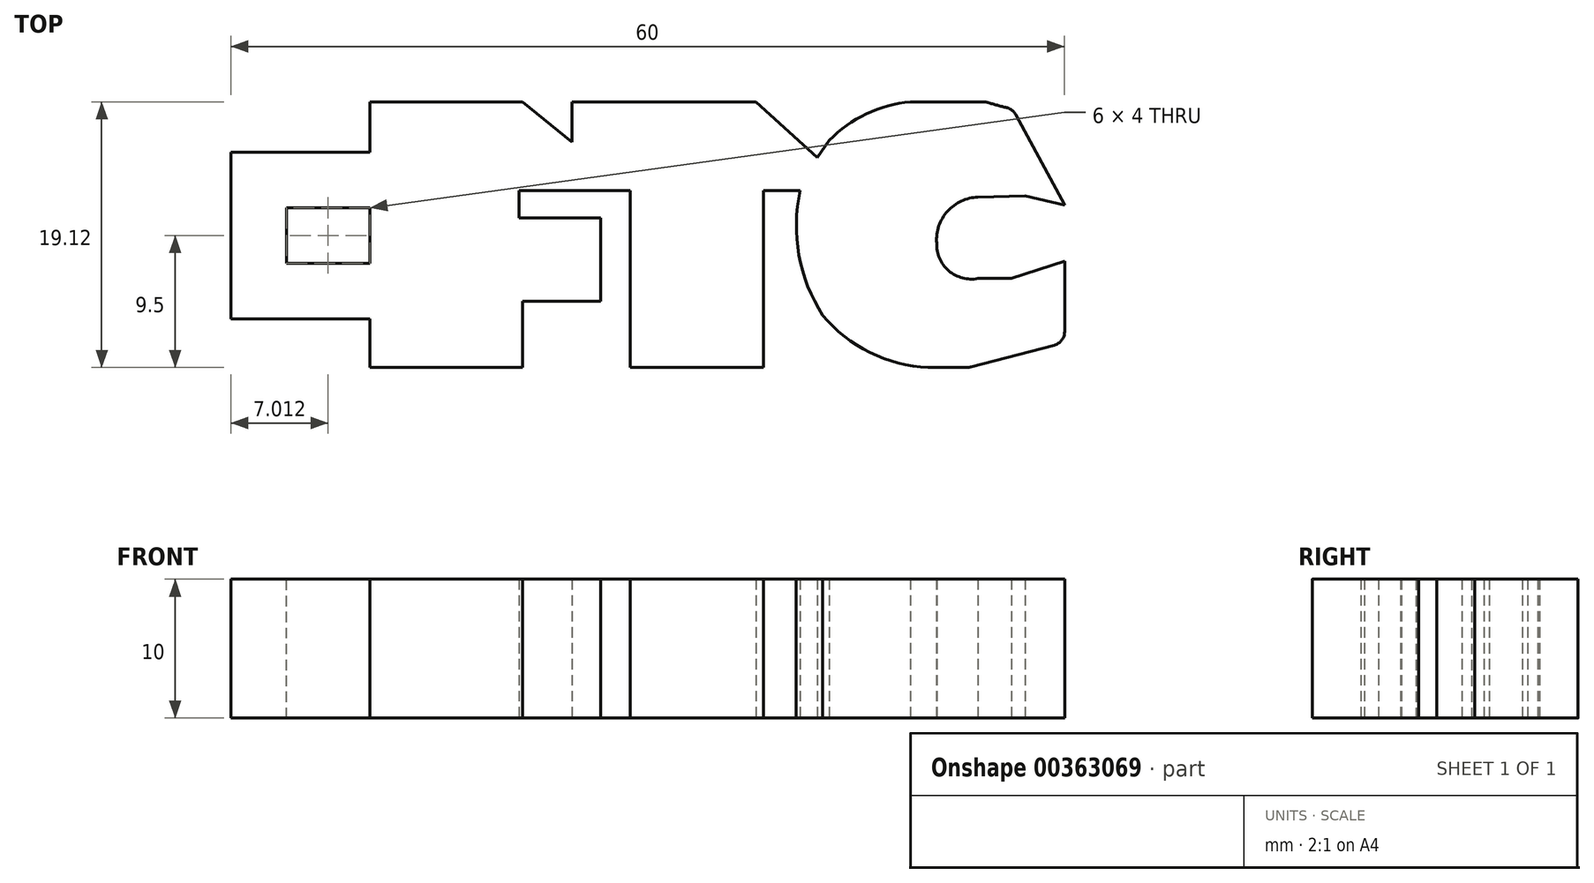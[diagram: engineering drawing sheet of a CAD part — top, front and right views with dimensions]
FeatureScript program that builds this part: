
annotation { "Feature Type Name" : "Feature", "Feature Type Description" : "" }
export const myFeature = defineFeature(function(context is Context, id is Id, definition is map)
    precondition{}
    {
        {
            var Q0;
            Q0=qCreatedBy(makeId("Top.planeOp"),FACE);
            var sketch = newSketch(context, id + "F0", { "sketchPlane" : qUnion([Q0])});
            skLineSegment(sketch, "E0", {"start": v(-22.32, 9.12) * mm, "end": v(-11.34, 9.12) * mm});
            skLineSegment(sketch, "E1", {"start": v(-22.32, 9.12) * mm, "end": v(-22.32, -10) * mm});
            skLineSegment(sketch, "E2", {"start": v(-22.32, -10) * mm, "end": v(-11.33, -10) * mm});
            skLineSegment(sketch, "E3", {"start": v(27.68, 1.7) * mm, "end": v(23.95, 8.6) * mm});
            skLineSegment(sketch, "E4", {"start": v(-7.76, 6.22) * mm, "end": v(-11.34, 9.12) * mm});
            skLineSegment(sketch, "E5", {"start": v(-7.76, 9.12) * mm, "end": v(-7.76, 6.22) * mm});
            skLineSegment(sketch, "E6", {"start": v(9.88, 5.1) * mm, "end": v(5.48, 9.12) * mm});
            skLineSegment(sketch, "E7", {"start": v(-11.56, 2.74) * mm, "end": v(-3.57, 2.74) * mm});
            skLineSegment(sketch, "E8", {"start": v(-11.56, 0.76) * mm, "end": v(-5.71, 0.76) * mm});
            skLineSegment(sketch, "E9", {"start": v(-11.56, 2.74) * mm, "end": v(-11.56, 0.76) * mm});
            skLineSegment(sketch, "E10", {"start": v(6.01, 2.74) * mm, "end": v(8.65, 2.74) * mm});
            skArc(sketch, "E11", {"start": v(22.01, 9.12) * mm, "mid": v(22.98, 8.84) * mm, "end": v(23.95, 8.6) * mm});
            skLineSegment(sketch, "E12", {"start": v(9.88, 5.1) * mm, "end": v(10.76, 6.34) * mm});
            skArc(sketch, "E13", {"start": v(16.58, 9.12) * mm, "mid": v(13.42, 8.26) * mm, "end": v(10.76, 6.34) * mm});
            skLineSegment(sketch, "E14", {"start": v(-11.33, -5.25) * mm, "end": v(-5.71, -5.25) * mm});
            skLineSegment(sketch, "E15", {"start": v(-11.33, -10) * mm, "end": v(-11.33, -5.25) * mm});
            skLineSegment(sketch, "E16", {"start": v(-3.57, 2.74) * mm, "end": v(-3.57, -10) * mm});
            skLineSegment(sketch, "E17", {"start": v(27.68, -8.2) * mm, "end": v(20.82, -10) * mm});
            skArc(sketch, "E18", {"start": v(8.65, 2.74) * mm, "mid": v(8.57, -1.91) * mm, "end": v(10.28, -6.24) * mm});
            skArc(sketch, "E19", {"start": v(10.28, -6.24) * mm, "mid": v(14.06, -9.1) * mm, "end": v(18.73, -10) * mm});
            skArc(sketch, "E20", {"start": v(21.45, 2.26) * mm, "mid": v(19.26, 1.25) * mm, "end": v(18.48, -1.04) * mm});
            skArc(sketch, "E21", {"start": v(18.48, -1.04) * mm, "mid": v(19.35, -3.04) * mm, "end": v(21.45, -3.6) * mm});
            skLineSegment(sketch, "E22", {"start": v(21.45, -3.6) * mm, "end": v(23.85, -3.6) * mm});
            skLineSegment(sketch, "E23", {"start": v(23.85, -3.6) * mm, "end": v(27.68, -2.34) * mm});
            skLineSegment(sketch, "E24", {"start": v(21.45, 2.26) * mm, "end": v(24.84, 2.36) * mm});
            skLineSegment(sketch, "E25", {"start": v(24.84, 2.36) * mm, "end": v(27.68, 1.68) * mm});
            skLineSegment(sketch, "E26", {"start": v(6.01, 2.74) * mm, "end": v(6.01, -10) * mm});
            skPoint(sketch, "E27.orphan", {"position": v(-11.56, 0) * mm});
            skLineSegment(sketch, "E28.trimOffspring", {"start": v(-5.71, 0.76) * mm, "end": v(-5.71, -5.25) * mm});
            skPoint(sketch, "E29.orphan", {"position": v(-2.04, 2.74) * mm});
            skPoint(sketch, "E30.orphan", {"position": v(-22.32, -12.38) * mm});
            skPoint(sketch, "E31.orphan", {"position": v(-26.16, -10) * mm});
            skPoint(sketch, "E32.orphan", {"position": v(5.02, 2.74) * mm});
            skPoint(sketch, "E33.orphan", {"position": v(10.28, 2.74) * mm});
            skLineSegment(sketch, "E34.trimOffspring", {"start": v(27.68, -8.2) * mm, "end": v(27.68, -2.34) * mm});
            skPoint(sketch, "E35.start.orphan", {"position": v(27.68, -12.38) * mm});
            skLineSegment(sketch, "E36.trimOffspring", {"start": v(17.9, -10) * mm, "end": v(20.82, -10) * mm});
            skLineSegment(sketch, "E37.trimOffspring", {"start": v(-3.57, -10) * mm, "end": v(6.01, -10) * mm});
            skLineSegment(sketch, "E38.trimOffspring", {"start": v(27.68, 1.68) * mm, "end": v(27.68, 1.7) * mm});
            skPoint(sketch, "E39.orphan", {"position": v(27.68, 15.76) * mm});
            skLineSegment(sketch, "E40.trimOffspring", {"start": v(-7.76, 9.12) * mm, "end": v(5.48, 9.12) * mm});
            skLineSegment(sketch, "E41.trimOffspring", {"start": v(16.58, 9.12) * mm, "end": v(22.01, 9.12) * mm});
            skSolve(sketch);
        }
        {
            var Q0;
            Q0=makeQuery(id+"F0.imprint","IMPRINT",FACE,{"disambiguationData":[TD([[makeQuery(id+"F0.imprint","IMPRINT",EDGE,{"derivedFrom":sQuery(id+"F0.wireOp",EDGE,"E0")}),-1.0]])]});
            extrude(context, id + "F1", {"entities" : qUnion([Q0]), "depth" : 10 * mm});
        }
        {
            var Q0;
            Q0=makeQuery(id+"F1.opExtrude","SWEPT_EDGE",EDGE,{"disambiguationData":[OSD([sQuery(id+"F0.wireOp",EDGE,"E3"),sQuery(id+"F0.wireOp",EDGE,"E11")])]});
            var Q1;
            Q1=makeQuery(id+"F1.opExtrude","SWEPT_EDGE",EDGE,{"disambiguationData":[OSD([sQuery(id+"F0.wireOp",EDGE,"E11"),sQuery(id+"F0.wireOp",EDGE,"E41.trimOffspring")])]});
            fillet(context, id + "F2", {"entities" : qUnion([Q0, Q1]), "radius" : 1 * mm, "tangentPropagation" : true, "allowEdgeOverflow" : false});
        }
        {
            var Q0;
            Q0=makeQuery(id+"F1.opExtrude","SWEPT_EDGE",EDGE,{"disambiguationData":[OSD([sQuery(id+"F0.wireOp",EDGE,"E19"),sQuery(id+"F0.wireOp",EDGE,"E36.trimOffspring")])]});
            var Q1;
            Q1=makeQuery(id+"F1.opExtrude","SWEPT_EDGE",EDGE,{"disambiguationData":[OSD([sQuery(id+"F0.wireOp",EDGE,"E17"),sQuery(id+"F0.wireOp",EDGE,"E36.trimOffspring")])]});
            fillet(context, id + "F3", {"entities" : qUnion([Q0, Q1]), "radius" : 1 * mm, "tangentPropagation" : true, "allowEdgeOverflow" : false});
        }
        {
            var Q0;
            Q0=makeQuery(id+"F1.opExtrude","SWEPT_EDGE",EDGE,{"disambiguationData":[OSD([sQuery(id+"F0.wireOp",EDGE,"E17"),sQuery(id+"F0.wireOp",EDGE,"E34.trimOffspring")])]});
            fillet(context, id + "F4", {"entities" : qUnion([Q0]), "radius" : 1 * mm, "tangentPropagation" : true, "allowEdgeOverflow" : false});
        }
        {
            var Q0;
            Q0=makeQuery(id+"F1.opExtrude","SWEPT_FACE",FACE,{"disambiguationData":[OSD([sQuery(id+"F0.wireOp",EDGE,"E1")])]});
            var sketch = newSketch(context, id + "F5", { "sketchPlane" : qUnion([Q0])});
            skLineSegment(sketch, "E42.bottom", {"start": v(-5.5, 10) * mm, "end": v(6.5, 10) * mm});
            skLineSegment(sketch, "E42.top", {"start": v(-5.5, 0) * mm, "end": v(6.5, 0) * mm});
            skLineSegment(sketch, "E42.left", {"start": v(-5.5, 10) * mm, "end": v(-5.5, 0) * mm});
            skLineSegment(sketch, "E42.right", {"start": v(6.5, 10) * mm, "end": v(6.5, 0) * mm});
            skSolve(sketch);
        }
        {
            var Q0;
            Q0=makeQuery(id+"F5.imprint","IMPRINT",FACE,{"disambiguationData":[TD([[makeQuery(id+"F5.imprint","IMPRINT",EDGE,{"derivedFrom":sQuery(id+"F5.wireOp",EDGE,"E42.bottom")}),-1.0]])]});
            extrude(context, id + "F6", {"entities" : qUnion([Q0]), "operationType" : NewBodyOperationType.ADD, "depth" : 10 * mm});
        }
        {
            var Q0;
            Q0=makeQuery(id+"F6.opExtrude","SWEPT_FACE",FACE,{"disambiguationData":[OSD([sQuery(id+"F5.wireOp",EDGE,"E42.bottom")])]});
            var sketch = newSketch(context, id + "F7", { "sketchPlane" : qUnion([Q0])});
            skLineSegment(sketch, "E43.bottom", {"start": v(-28.3, 1.5) * mm, "end": v(-22.3, 1.5) * mm});
            skLineSegment(sketch, "E43.top", {"start": v(-28.3, -2.5) * mm, "end": v(-22.3, -2.5) * mm});
            skLineSegment(sketch, "E43.left", {"start": v(-28.3, 1.5) * mm, "end": v(-28.3, -2.5) * mm});
            skLineSegment(sketch, "E43.right", {"start": v(-22.3, 1.5) * mm, "end": v(-22.3, -2.5) * mm});
            skSolve(sketch);
        }
        {
            var Q0;
            Q0=makeQuery(id+"F7.imprint","IMPRINT",FACE,{"disambiguationData":[TD([[makeQuery(id+"F7.imprint","IMPRINT",EDGE,{"derivedFrom":sQuery(id+"F7.wireOp",EDGE,"E43.bottom")}),-1.0]])]});
            extrude(context, id + "F8", {"entities" : qUnion([Q0]), "operationType" : NewBodyOperationType.REMOVE, "oppositeDirection" : true, "depth" : 25 * mm});
        }
    });
